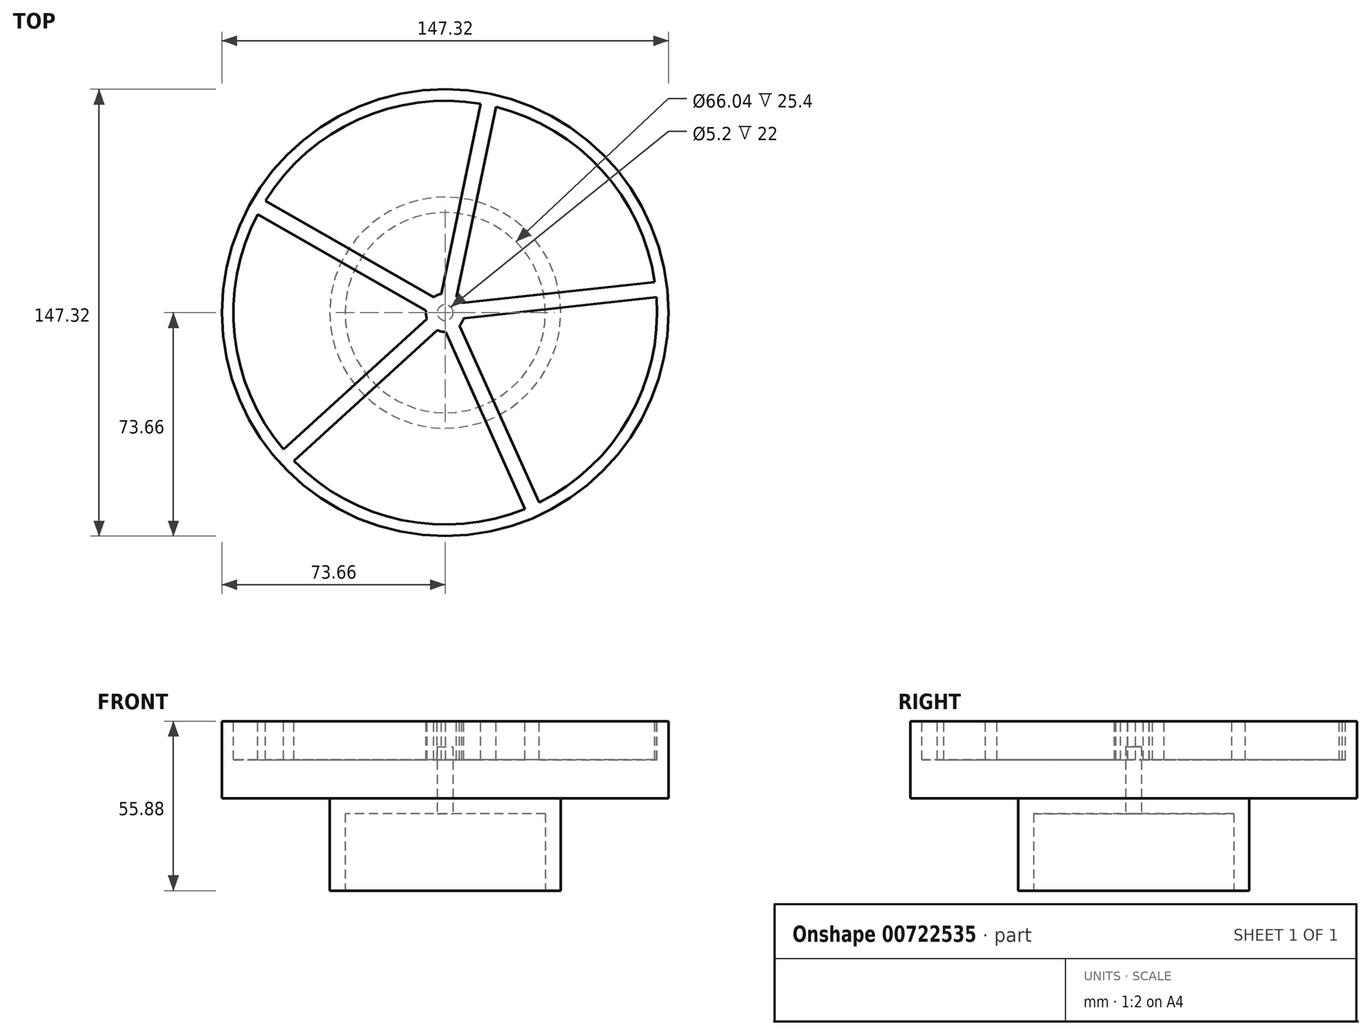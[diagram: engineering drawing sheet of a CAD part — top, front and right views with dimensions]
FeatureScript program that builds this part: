
annotation { "Feature Type Name" : "Feature", "Feature Type Description" : "" }
export const myFeature = defineFeature(function(context is Context, id is Id, definition is map)
    precondition{}
    {
        {
            var Q0;
            Q0=qCreatedBy(makeId("Top.planeOp"),FACE);
            var sketch = newSketch(context, id + "F0", { "sketchPlane" : qUnion([Q0])});
            skCircle(sketch, "E0", {"center": v(0, 0) * mm, "radius": 38.1 * mm});
            skCircle(sketch, "E1", {"center": v(0, 0) * mm, "radius": 33.02 * mm});
            skSolve(sketch);
        }
        {
            var Q0;
            Q0=makeQuery(id+"F0.imprint","IMPRINT",FACE,{"disambiguationData":[TD([[makeQuery(id+"F0.imprint","IMPRINT",EDGE,{"derivedFrom":sQuery(id+"F0.wireOp",EDGE,"E0")}),1.0]])]});
            extrude(context, id + "F1", {"entities" : qUnion([Q0]), "depth" : 25.4 * mm, "offsetDistance" : 25.4 * mm});
        }
        {
            var Q0;
            Q0=makeQuery(id+"F1.opExtrude","CAP_FACE",FACE,{"disambiguationData":[OSD([sQuery(id+"F0.wireOp",EDGE,"E0"),sQuery(id+"F0.wireOp",EDGE,"E1")])],"isStart":false});
            var sketch = newSketch(context, id + "F2", { "sketchPlane" : qUnion([Q0])});
            skCircle(sketch, "E2", {"center": v(0, 0) * mm, "radius": 38.1 * mm});
            skSolve(sketch);
        }
        {
            var Q0;
            Q0 = qSketchRegion(id + "F2", true);
            extrude(context, id + "F3", {"entities" : qUnion([Q0]), "operationType" : NewBodyOperationType.ADD, "depth" : 5.08 * mm, "offsetDistance" : 25.4 * mm});
        }
        {
            var Q0;
            Q0=makeQuery(id+"F3.opExtrude","CAP_FACE",FACE,{"disambiguationData":[OSD([sQuery(id+"F2.wireOp",EDGE,"E2")])],"isStart":false});
            var sketch = newSketch(context, id + "F4", { "sketchPlane" : qUnion([Q0])});
            skCircle(sketch, "E3", {"center": v(0, 0) * mm, "radius": 73.66 * mm});
            skSolve(sketch);
        }
        {
            var Q0;
            Q0=makeQuery(id+"F4.imprint","IMPRINT",FACE,{"disambiguationData":[TD([[makeQuery(id+"F4.imprint","IMPRINT",EDGE,{"derivedFrom":sQuery(id+"F4.wireOp",EDGE,"E3")}),1.0]])]});
            var Q1;
            Q1=makeQuery(id+"F4.imprint","IMPRINT",FACE,{"disambiguationData":[TD([[makeQuery(id+"F4.imprint","IMPRINT",EDGE,{"derivedFrom":makeQuery(id+"F3.opExtrude","CAP_EDGE",EDGE,{"disambiguationData":[OSD([sQuery(id+"F2.wireOp",EDGE,"E2")])],"isStart":false})}),1.0]])]});
            extrude(context, id + "F5", {"entities" : qUnion([Q0, Q1]), "operationType" : NewBodyOperationType.ADD, "depth" : 25.4 * mm, "offsetDistance" : 25.4 * mm});
        }
        {
            var Q0;
            Q0=makeQuery(id+"F5.opExtrude","CAP_FACE",FACE,{"disambiguationData":[OSD([sQuery(id+"F4.wireOp",EDGE,"E3")])],"isStart":false});
            var sketch = newSketch(context, id + "F6", { "sketchPlane" : qUnion([Q0])});
            skCircle(sketch, "E4", {"center": v(0, 0) * mm, "radius": 6.35 * mm});
            skCircle(sketch, "E5", {"center": v(0, 0) * mm, "radius": 69.85 * mm});
            skCircle(sketch, "E6", {"center": v(0, 0) * mm, "radius": 73.66 * mm});
            skPoint(sketch, "E7.0.midPoint", {"position": v(49.88, -28.52) * mm});
            skLineSegment(sketch, "E8", {"start": v(14.48, 69.54) * mm, "end": v(0, 0) * mm});
            skLineSegment(sketch, "E9", {"start": v(70.6, 7.72) * mm, "end": v(0, 0) * mm});
            skLineSegment(sketch, "E10", {"start": v(29.16, -64.76) * mm, "end": v(0, 0) * mm});
            skLineSegment(sketch, "E11", {"start": v(-52.58, -47.75) * mm, "end": v(0, 0) * mm});
            skLineSegment(sketch, "E12", {"start": v(-61.66, 35.25) * mm, "end": v(0, 0) * mm});
            skLineSegment(sketch, "E13", {"start": v(-61.66, 35.25) * mm, "end": v(-62.92, 33.05) * mm});
            skLineSegment(sketch, "E14", {"start": v(-62.92, 33.05) * mm, "end": v(-60.4, 37.46) * mm});
            skLineSegment(sketch, "E15", {"start": v(-60.4, 37.46) * mm, "end": v(-3.8, 5.1) * mm});
            skLineSegment(sketch, "E16", {"start": v(-62.92, 33.05) * mm, "end": v(-6.31, 0.68) * mm});
            skLineSegment(sketch, "E17", {"start": v(-52.58, -47.75) * mm, "end": v(-54.3, -45.87) * mm});
            skLineSegment(sketch, "E18", {"start": v(-54.3, -45.87) * mm, "end": v(-6.02, -2.03) * mm});
            skLineSegment(sketch, "E19", {"start": v(-6.02, -2.03) * mm, "end": v(-2.6, -5.8) * mm});
            skLineSegment(sketch, "E20", {"start": v(-2.6, -5.8) * mm, "end": v(-49.97, -48.8) * mm});
            skLineSegment(sketch, "E21", {"start": v(-49.97, -48.8) * mm, "end": v(-54.3, -45.87) * mm});
            skLineSegment(sketch, "E22", {"start": v(14.48, 69.54) * mm, "end": v(16.96, 69.02) * mm});
            skLineSegment(sketch, "E23", {"start": v(16.96, 69.02) * mm, "end": v(3.67, 5.18) * mm});
            skLineSegment(sketch, "E24", {"start": v(3.67, 5.18) * mm, "end": v(-1.3, 6.22) * mm});
            skLineSegment(sketch, "E25", {"start": v(-1.3, 6.22) * mm, "end": v(11.74, 68.86) * mm});
            skLineSegment(sketch, "E26", {"start": v(16.96, 69.02) * mm, "end": v(11.74, 68.86) * mm});
            skLineSegment(sketch, "E27", {"start": v(70.6, 7.72) * mm, "end": v(70.88, 5.2) * mm});
            skLineSegment(sketch, "E28", {"start": v(70.88, 5.2) * mm, "end": v(6.06, -1.9) * mm});
            skLineSegment(sketch, "E29", {"start": v(70.88, 5.2) * mm, "end": v(70.33, 10.25) * mm});
            skLineSegment(sketch, "E30", {"start": v(70.33, 10.25) * mm, "end": v(5.5, 3.16) * mm});
            skLineSegment(sketch, "E31", {"start": v(29.16, -64.76) * mm, "end": v(31.48, -63.72) * mm});
            skLineSegment(sketch, "E32", {"start": v(31.48, -63.72) * mm, "end": v(4.7, -4.26) * mm});
            skLineSegment(sketch, "E33", {"start": v(31.48, -63.72) * mm, "end": v(26.85, -65.8) * mm});
            skLineSegment(sketch, "E34", {"start": v(26.85, -65.8) * mm, "end": v(0, -6.19) * mm});
            skSolve(sketch);
        }
        {
            var Q0;
            {var subQ0=sQuery(id+"F6.wireOp",EDGE,"E16");var subQ5=sQuery(id+"F6.wireOp",EDGE,"E5");var subQ6=makeQuery(id+"F6.imprint","INTERSECT",VERTEX,{"derivedFrom":[subQ5,subQ0]});Q0=makeQuery(id+"F6.imprint","IMPRINT",FACE,{"disambiguationData":[TD([[makeQuery(id+"F6.imprint","IMPRINT",EDGE,{"disambiguationData":[TD([[subQ6,-1.0]])],"derivedFrom":subQ5}),1.0]])]});}
            var Q1;
            {var subQ3=sQuery(id+"F6.wireOp",EDGE,"E25");Q1=makeQuery(id+"F6.imprint","IMPRINT",FACE,{"disambiguationData":[TD([[makeQuery(id+"F6.imprint","IMPRINT",EDGE,{"derivedFrom":subQ3}),1.0]])]});}
            var Q2;
            {var subQ3=sQuery(id+"F6.wireOp",EDGE,"E30");var subQ5=sQuery(id+"F6.wireOp",EDGE,"E5");var subQ7=makeQuery(id+"F6.imprint","INTERSECT",VERTEX,{"derivedFrom":[subQ5,subQ3]});Q2=makeQuery(id+"F6.imprint","IMPRINT",FACE,{"disambiguationData":[TD([[makeQuery(id+"F6.imprint","IMPRINT",EDGE,{"disambiguationData":[TD([[subQ7,-1.0]])],"derivedFrom":subQ5}),1.0]])]});}
            var Q3;
            {var subQ0=sQuery(id+"F6.wireOp",EDGE,"E28");var subQ1=sQuery(id+"F6.wireOp",EDGE,"E4");var subQ2=makeQuery(id+"F6.imprint","INTERSECT",VERTEX,{"derivedFrom":[subQ1,subQ0]});Q3=makeQuery(id+"F6.imprint","IMPRINT",FACE,{"disambiguationData":[TD([[makeQuery(id+"F6.imprint","IMPRINT",EDGE,{"disambiguationData":[TD([[subQ2,1.0]])],"derivedFrom":subQ1}),-1.0]])]});}
            var Q4;
            {var subQ0=sQuery(id+"F6.wireOp",EDGE,"E20");Q4=makeQuery(id+"F6.imprint","IMPRINT",FACE,{"disambiguationData":[TD([[makeQuery(id+"F6.imprint","IMPRINT",EDGE,{"derivedFrom":subQ0}),1.0]])]});}
            extrude(context, id + "F7", {"entities" : qUnion([Q0, Q1, Q2, Q3, Q4]), "operationType" : NewBodyOperationType.REMOVE, "oppositeDirection" : true, "depth" : 12.7 * mm, "offsetDistance" : 25.4 * mm});
        }
        {
            var Q0;
            Q0=makeQuery(id+"F3.opExtrude","CAP_FACE",FACE,{"disambiguationData":[OSD([sQuery(id+"F2.wireOp",EDGE,"E2")])],"isStart":true});
            var sketch = newSketch(context, id + "F8", { "sketchPlane" : qUnion([Q0])});
            skCircle(sketch, "E35", {"center": v(0, 0) * mm, "radius": 2.6 * mm});
            skSolve(sketch);
        }
        {
            var Q0;
            Q0=makeQuery(id+"F8.imprint","IMPRINT",FACE,{"disambiguationData":[TD([[makeQuery(id+"F8.imprint","IMPRINT",EDGE,{"derivedFrom":sQuery(id+"F8.wireOp",EDGE,"E35")}),1.0]])]});
            extrude(context, id + "F9", {"entities" : qUnion([Q0]), "operationType" : NewBodyOperationType.REMOVE, "oppositeDirection" : true, "depth" : 22 * mm, "offsetDistance" : 25.4 * mm});
        }
    });
